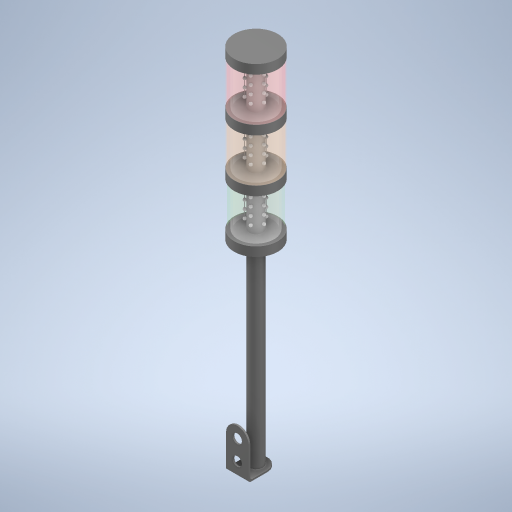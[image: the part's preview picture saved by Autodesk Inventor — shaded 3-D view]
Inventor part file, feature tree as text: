
AUTODESK INVENTOR PART (.ipt)
format: ipt  version: 2024 (Build 280153000, 153)  size: 786,944 bytes
history: native  units: in
note: dims shown in document units (in); Inventor stores cm internally (conversion verified against a paired STEP export)
features: other x23, extrude x3, sketch x3, projected_geometry x2, fillet x1, revolve x1
ambient origin geometry x8: Origin, YZ Plane, XZ Plane, XY Plane, X Axis, Y Axis, Z Axis, Center Point
bodies: Solid1 (feature_tree), Solid2 (feature_tree), Solid3 (feature_tree), Solid4 (feature_tree), Solid5 (feature_tree), Solid6 (feature_tree), Solid7 (feature_tree), Solid8 (feature_tree), Solid9 (feature_tree), Solid10 (feature_tree), Solid11 (feature_tree), Solid12 (feature_tree), Solid13 (feature_tree), Solid14 (feature_tree), Solid15 (feature_tree), Solid16 (feature_tree), Solid17 (feature_tree), Solid18 (feature_tree), Solid19 (feature_tree), Solid20 (feature_tree), Solid21 (feature_tree), Solid22 (feature_tree)
feature tree (33):
  other  "Axis1"
  other  "Plane1"
  extrude  "Extrusion1"  Depth=0.1in TaperAngle=0.0deg
  extrude  "Extrusion2"  Depth=0.125in
  extrude  "Extrusion3"  [1 undecoded]
  fillet  "Fillet1"  [1 undecoded]
  sketch  "Sketch1"  dims[d0=12.0in d1=0.0in d2=0.1in d3=0.0in]
  projected_geometry  "Projected Loop1"
  sketch  "Sketch2"  dims[d4=0.1in d5=0.0in d6=0.125in]
  projected_geometry  "Projected Loop2"
  sketch  "Sketch3"
  other  "Boss-Extrude2"
  other  "Boss-Extrude4"
  other  "Boss-Extrude6"
  other  "Boss-Extrude8"
  revolve  "Revolve2"  [1 undecoded]
  other  "Boss-Extrude9"
  other  "CirPattern3[1]"
  other  "CirPattern3[2]"
  other  "CirPattern3[3]"
  other  "CirPattern3[4]"
  other  "LPattern2[1]"
  other  "LPattern2[2]"
  other  "LPattern2[3]"
  other  "LPattern2[4]"
  other  "LPattern2[5]"
  other  "LPattern2[6]"
  other  "LPattern2[7]"
  other  "LPattern2[8]"
  other  "LPattern2[9]"
  other  "LPattern2[10]"
  other  "LPattern2[11]"
  other  "LPattern2[12]"
note: 3 required parameter values undecoded (feature->parameter linkage not recoverable at this tier; creation-order binding heuristic only, values carry confidence <= 0.55)
